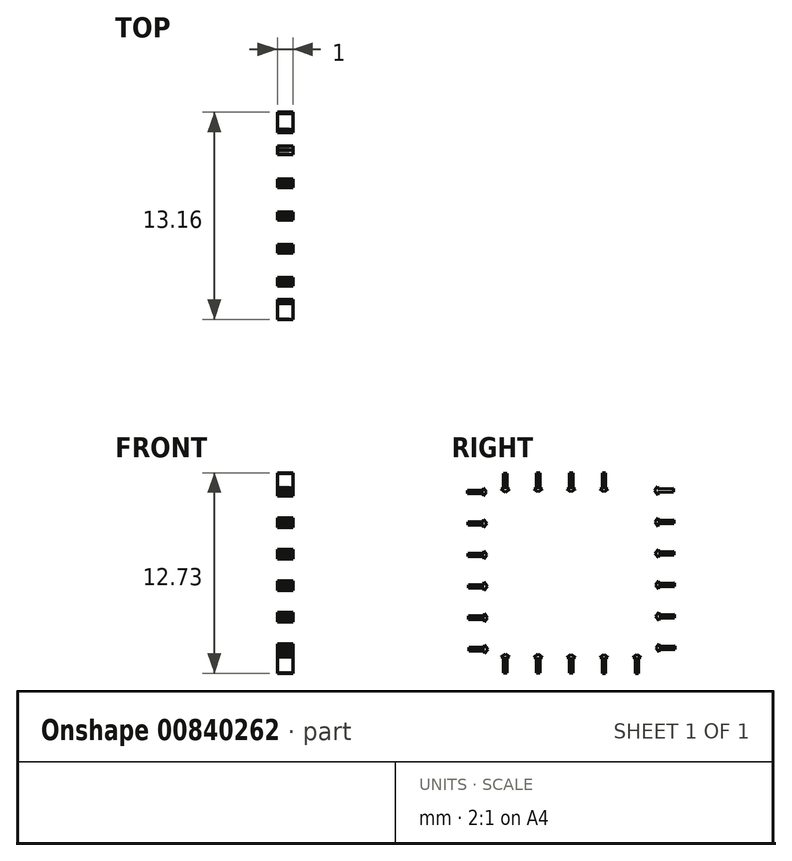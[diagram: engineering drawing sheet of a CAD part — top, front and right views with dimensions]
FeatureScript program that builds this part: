
annotation { "Feature Type Name" : "Feature", "Feature Type Description" : "" }
export const myFeature = defineFeature(function(context is Context, id is Id, definition is map)
    precondition{}
    {
        {
            var Q0;
            Q0=qCreatedBy(makeId("Right.planeOp"),FACE);
            var sketch = newSketch(context, id + "F0", { "sketchPlane" : qUnion([Q0])});
            skLineSegment(sketch, "E0.0.4.1", {"start": v(0.27, -10.76) * mm, "end": v(-0.73, -10.76) * mm});
            skLineSegment(sketch, "E1", {"start": v(1.47, -11.15) * mm, "end": v(1.47, -12.15) * mm});
            skLineSegment(sketch, "E2", {"start": v(-0.73, -10.76) * mm, "end": v(-0.73, -10.55) * mm});
            skLineSegment(sketch, "E3", {"start": v(-0.73, -10.55) * mm, "end": v(0.27, -10.55) * mm});
            skLineSegment(sketch, "E4", {"start": v(0.27, -10.55) * mm, "end": v(0.27, -10.39) * mm});
            skLineSegment(sketch, "E5", {"start": v(0.27, -10.76) * mm, "end": v(0.27, -10.92) * mm});
            skLineSegment(sketch, "E6", {"start": v(0.47, -10.65) * mm, "end": v(0.27, -10.39) * mm});
            skLineSegment(sketch, "E7", {"start": v(0.47, -10.65) * mm, "end": v(0.27, -10.92) * mm});
            skLineSegment(sketch, "E8.0.1.0", {"start": v(-0.75, -8.55) * mm, "end": v(0.25, -8.55) * mm});
            skLineSegment(sketch, "E8.0.1.1", {"start": v(0.25, -8.76) * mm, "end": v(-0.75, -8.76) * mm});
            skLineSegment(sketch, "E8.0.1.2", {"start": v(0.25, -8.76) * mm, "end": v(0.25, -8.92) * mm});
            skLineSegment(sketch, "E8.0.1.3", {"start": v(0.45, -8.65) * mm, "end": v(0.25, -8.92) * mm});
            skLineSegment(sketch, "E8.0.1.4", {"start": v(-0.75, -8.76) * mm, "end": v(-0.75, -8.55) * mm});
            skLineSegment(sketch, "E8.0.1.5", {"start": v(0.45, -8.65) * mm, "end": v(0.25, -8.39) * mm});
            skLineSegment(sketch, "E8.0.1.6", {"start": v(0.25, -8.55) * mm, "end": v(0.25, -8.39) * mm});
            skLineSegment(sketch, "E8.0.2.0", {"start": v(-0.77, -6.55) * mm, "end": v(0.24, -6.55) * mm});
            skLineSegment(sketch, "E8.0.2.1", {"start": v(0.24, -6.76) * mm, "end": v(-0.77, -6.76) * mm});
            skLineSegment(sketch, "E8.0.2.2", {"start": v(0.24, -6.76) * mm, "end": v(0.24, -6.92) * mm});
            skLineSegment(sketch, "E8.0.2.3", {"start": v(0.44, -6.66) * mm, "end": v(0.24, -6.92) * mm});
            skLineSegment(sketch, "E8.0.2.4", {"start": v(-0.77, -6.76) * mm, "end": v(-0.77, -6.55) * mm});
            skLineSegment(sketch, "E8.0.2.5", {"start": v(0.44, -6.66) * mm, "end": v(0.24, -6.39) * mm});
            skLineSegment(sketch, "E8.0.2.6", {"start": v(0.24, -6.55) * mm, "end": v(0.24, -6.39) * mm});
            skLineSegment(sketch, "E8.0.3.0", {"start": v(-0.78, -4.55) * mm, "end": v(0.22, -4.55) * mm});
            skLineSegment(sketch, "E8.0.3.1", {"start": v(0.22, -4.76) * mm, "end": v(-0.78, -4.76) * mm});
            skLineSegment(sketch, "E8.0.3.2", {"start": v(0.22, -4.76) * mm, "end": v(0.22, -4.92) * mm});
            skLineSegment(sketch, "E8.0.3.3", {"start": v(0.42, -4.66) * mm, "end": v(0.22, -4.92) * mm});
            skLineSegment(sketch, "E8.0.3.4", {"start": v(-0.78, -4.76) * mm, "end": v(-0.78, -4.55) * mm});
            skLineSegment(sketch, "E8.0.3.5", {"start": v(0.42, -4.66) * mm, "end": v(0.22, -4.4) * mm});
            skLineSegment(sketch, "E8.0.3.6", {"start": v(0.22, -4.55) * mm, "end": v(0.22, -4.4) * mm});
            skLineSegment(sketch, "E8.0.4.0", {"start": v(-0.8, -2.55) * mm, "end": v(0.2, -2.55) * mm});
            skLineSegment(sketch, "E8.0.4.1", {"start": v(0.2, -2.76) * mm, "end": v(-0.8, -2.76) * mm});
            skLineSegment(sketch, "E8.0.4.2", {"start": v(0.2, -2.76) * mm, "end": v(0.2, -2.92) * mm});
            skLineSegment(sketch, "E8.0.4.3", {"start": v(0.4, -2.66) * mm, "end": v(0.2, -2.92) * mm});
            skLineSegment(sketch, "E8.0.4.4", {"start": v(-0.8, -2.76) * mm, "end": v(-0.8, -2.55) * mm});
            skLineSegment(sketch, "E8.0.4.5", {"start": v(0.4, -2.66) * mm, "end": v(0.2, -2.4) * mm});
            skLineSegment(sketch, "E8.0.4.6", {"start": v(0.2, -2.55) * mm, "end": v(0.2, -2.4) * mm});
            skLineSegment(sketch, "E8.0.5.0", {"start": v(-0.81, -0.55) * mm, "end": v(0.2, -0.55) * mm});
            skLineSegment(sketch, "E8.0.5.1", {"start": v(0.2, -0.77) * mm, "end": v(-0.81, -0.77) * mm});
            skLineSegment(sketch, "E8.0.5.2", {"start": v(0.2, -0.77) * mm, "end": v(0.2, -0.93) * mm});
            skLineSegment(sketch, "E8.0.5.3", {"start": v(0.39, -0.66) * mm, "end": v(0.2, -0.93) * mm});
            skLineSegment(sketch, "E8.0.5.4", {"start": v(-0.81, -0.77) * mm, "end": v(-0.81, -0.55) * mm});
            skLineSegment(sketch, "E8.0.5.5", {"start": v(0.39, -0.66) * mm, "end": v(0.2, -0.4) * mm});
            skLineSegment(sketch, "E8.0.5.6", {"start": v(0.2, -0.55) * mm, "end": v(0.2, -0.4) * mm});
            skLineSegment(sketch, "E8.direction1", {"start": v(-0.73, -10.76) * mm, "end": v(24.27, -10.76) * mm, "construction": true});
            skLineSegment(sketch, "E8.direction2", {"start": v(-0.73, -10.76) * mm, "end": v(-0.75, -8.76) * mm, "construction": true});
            skLineSegment(sketch, "E9", {"start": v(1.47, -12.15) * mm, "end": v(1.68, -12.15) * mm});
            skLineSegment(sketch, "E10", {"start": v(1.68, -12.15) * mm, "end": v(1.68, -11.15) * mm});
            skLineSegment(sketch, "E11", {"start": v(1.47, -11.15) * mm, "end": v(1.3, -11.15) * mm});
            skLineSegment(sketch, "E12", {"start": v(1.68, -11.15) * mm, "end": v(1.84, -11.15) * mm});
            skLineSegment(sketch, "E13", {"start": v(1.58, -10.95) * mm, "end": v(1.3, -11.15) * mm});
            skLineSegment(sketch, "E14", {"start": v(1.58, -10.95) * mm, "end": v(1.84, -11.15) * mm});
            skLineSegment(sketch, "E15.1.0.0", {"start": v(3.56, -12.16) * mm, "end": v(3.77, -12.16) * mm});
            skLineSegment(sketch, "E15.1.0.1", {"start": v(3.67, -10.96) * mm, "end": v(3.4, -11.16) * mm});
            skLineSegment(sketch, "E15.1.0.2", {"start": v(3.56, -11.16) * mm, "end": v(3.4, -11.16) * mm});
            skLineSegment(sketch, "E15.1.0.3", {"start": v(3.77, -12.16) * mm, "end": v(3.77, -11.16) * mm});
            skLineSegment(sketch, "E15.1.0.4", {"start": v(3.67, -10.96) * mm, "end": v(3.93, -11.16) * mm});
            skLineSegment(sketch, "E15.1.0.5", {"start": v(3.56, -11.16) * mm, "end": v(3.56, -12.16) * mm});
            skLineSegment(sketch, "E15.1.0.6", {"start": v(3.77, -11.16) * mm, "end": v(3.93, -11.16) * mm});
            skLineSegment(sketch, "E15.2.0.0", {"start": v(5.65, -12.17) * mm, "end": v(5.86, -12.17) * mm});
            skLineSegment(sketch, "E15.2.0.1", {"start": v(5.76, -10.96) * mm, "end": v(5.5, -11.16) * mm});
            skLineSegment(sketch, "E15.2.0.2", {"start": v(5.65, -11.16) * mm, "end": v(5.5, -11.16) * mm});
            skLineSegment(sketch, "E15.2.0.3", {"start": v(5.86, -12.17) * mm, "end": v(5.86, -11.16) * mm});
            skLineSegment(sketch, "E15.2.0.4", {"start": v(5.76, -10.96) * mm, "end": v(6.02, -11.16) * mm});
            skLineSegment(sketch, "E15.2.0.5", {"start": v(5.65, -11.16) * mm, "end": v(5.65, -12.17) * mm});
            skLineSegment(sketch, "E15.2.0.6", {"start": v(5.86, -11.16) * mm, "end": v(6.02, -11.16) * mm});
            skLineSegment(sketch, "E15.3.0.0", {"start": v(7.74, -12.18) * mm, "end": v(7.95, -12.18) * mm});
            skLineSegment(sketch, "E15.3.0.1", {"start": v(7.85, -10.97) * mm, "end": v(7.58, -11.17) * mm});
            skLineSegment(sketch, "E15.3.0.2", {"start": v(7.74, -11.17) * mm, "end": v(7.58, -11.17) * mm});
            skLineSegment(sketch, "E15.3.0.3", {"start": v(7.95, -12.18) * mm, "end": v(7.95, -11.17) * mm});
            skLineSegment(sketch, "E15.3.0.4", {"start": v(7.85, -10.97) * mm, "end": v(8.11, -11.17) * mm});
            skLineSegment(sketch, "E15.3.0.5", {"start": v(7.74, -11.17) * mm, "end": v(7.74, -12.18) * mm});
            skLineSegment(sketch, "E15.3.0.6", {"start": v(7.95, -11.17) * mm, "end": v(8.11, -11.17) * mm});
            skLineSegment(sketch, "E15.4.0.0", {"start": v(9.83, -12.18) * mm, "end": v(10.04, -12.18) * mm});
            skLineSegment(sketch, "E15.4.0.1", {"start": v(9.94, -10.98) * mm, "end": v(9.67, -11.18) * mm});
            skLineSegment(sketch, "E15.4.0.2", {"start": v(9.83, -11.18) * mm, "end": v(9.67, -11.18) * mm});
            skLineSegment(sketch, "E15.4.0.3", {"start": v(10.04, -12.18) * mm, "end": v(10.04, -11.18) * mm});
            skLineSegment(sketch, "E15.4.0.4", {"start": v(9.94, -10.98) * mm, "end": v(10.2, -11.18) * mm});
            skLineSegment(sketch, "E15.4.0.5", {"start": v(9.83, -11.18) * mm, "end": v(9.83, -12.18) * mm});
            skLineSegment(sketch, "E15.4.0.6", {"start": v(10.04, -11.18) * mm, "end": v(10.2, -11.18) * mm});
            skLineSegment(sketch, "E15.direction1", {"start": v(1.47, -12.15) * mm, "end": v(3.56, -12.16) * mm, "construction": true});
            skLineSegment(sketch, "E16.MirrorCS", {"start": v(11.14, -10.57) * mm, "end": v(11.35, -10.83) * mm});
            skLineSegment(sketch, "E17.MirrorCS", {"start": v(11.14, -10.57) * mm, "end": v(11.34, -10.3) * mm});
            skLineSegment(sketch, "E18.MirrorCS", {"start": v(11.34, -10.67) * mm, "end": v(11.35, -10.83) * mm});
            skLineSegment(sketch, "E19.MirrorCS", {"start": v(11.34, -10.46) * mm, "end": v(11.34, -10.3) * mm});
            skLineSegment(sketch, "E20.MirrorCS", {"start": v(11.33, -8.67) * mm, "end": v(11.33, -8.83) * mm});
            skLineSegment(sketch, "E21.MirrorCS", {"start": v(11.13, -8.57) * mm, "end": v(11.32, -8.3) * mm});
            skLineSegment(sketch, "E22.MirrorCS", {"start": v(12.35, -10.65) * mm, "end": v(12.35, -10.44) * mm});
            skLineSegment(sketch, "E23.MirrorCS", {"start": v(11.33, -8.46) * mm, "end": v(11.32, -8.3) * mm});
            skLineSegment(sketch, "E24.MirrorCS", {"start": v(11.06, -0.57) * mm, "end": v(11.26, -0.3) * mm});
            skLineSegment(sketch, "E25.MirrorCS", {"start": v(11.06, -0.57) * mm, "end": v(11.27, -0.84) * mm});
            skLineSegment(sketch, "E26.MirrorCS", {"start": v(11.3, -4.46) * mm, "end": v(11.3, -4.3) * mm});
            skLineSegment(sketch, "E27.MirrorCS", {"start": v(11.26, -0.68) * mm, "end": v(11.27, -0.84) * mm});
            skLineSegment(sketch, "E28.MirrorCS", {"start": v(11.08, -2.57) * mm, "end": v(11.27, -2.3) * mm});
            skLineSegment(sketch, "E29.MirrorCS", {"start": v(11.11, -6.57) * mm, "end": v(11.3, -6.3) * mm});
            skLineSegment(sketch, "E30.MirrorCS", {"start": v(11.1, -4.57) * mm, "end": v(11.3, -4.3) * mm});
            skLineSegment(sketch, "E31.MirrorCS", {"start": v(11.3, -4.67) * mm, "end": v(11.3, -4.83) * mm});
            skLineSegment(sketch, "E32.MirrorCS", {"start": v(12.33, -8.65) * mm, "end": v(12.33, -8.44) * mm});
            skLineSegment(sketch, "E33.MirrorCS", {"start": v(11.3, -6.46) * mm, "end": v(11.3, -6.3) * mm});
            skLineSegment(sketch, "E34.MirrorCS", {"start": v(11.31, -6.67) * mm, "end": v(11.31, -6.83) * mm});
            skLineSegment(sketch, "E35.MirrorCS", {"start": v(11.1, -4.57) * mm, "end": v(11.3, -4.83) * mm});
            skLineSegment(sketch, "E36.MirrorCS", {"start": v(11.28, -2.67) * mm, "end": v(11.28, -2.83) * mm});
            skLineSegment(sketch, "E37.MirrorCS", {"start": v(11.11, -6.57) * mm, "end": v(11.31, -6.83) * mm});
            skLineSegment(sketch, "E38.MirrorCS", {"start": v(11.08, -2.57) * mm, "end": v(11.28, -2.83) * mm});
            skLineSegment(sketch, "E39.MirrorCS", {"start": v(11.13, -8.57) * mm, "end": v(11.33, -8.83) * mm});
            skLineSegment(sketch, "E40.MirrorCS", {"start": v(11.26, -0.46) * mm, "end": v(11.26, -0.3) * mm});
            skLineSegment(sketch, "E41.MirrorCS", {"start": v(12.3, -4.66) * mm, "end": v(12.3, -4.44) * mm});
            skLineSegment(sketch, "E42.MirrorCS", {"start": v(12.32, -6.66) * mm, "end": v(12.31, -6.44) * mm});
            skLineSegment(sketch, "E43.MirrorCS", {"start": v(12.27, -0.66) * mm, "end": v(12.27, -0.45) * mm});
            skLineSegment(sketch, "E44.MirrorCS", {"start": v(11.28, -2.46) * mm, "end": v(11.27, -2.3) * mm});
            skLineSegment(sketch, "E45.MirrorCS", {"start": v(12.28, -2.66) * mm, "end": v(12.28, -2.45) * mm});
            skLineSegment(sketch, "E46.MirrorCS", {"start": v(12.31, -6.44) * mm, "end": v(11.3, -6.46) * mm});
            skLineSegment(sketch, "E47.MirrorCS", {"start": v(11.3, -4.67) * mm, "end": v(12.3, -4.66) * mm});
            skLineSegment(sketch, "E48.MirrorCS", {"start": v(12.3, -4.44) * mm, "end": v(11.3, -4.46) * mm});
            skLineSegment(sketch, "E49.MirrorCS", {"start": v(12.35, -10.44) * mm, "end": v(11.34, -10.46) * mm});
            skLineSegment(sketch, "E50.MirrorCS", {"start": v(11.28, -2.67) * mm, "end": v(12.28, -2.66) * mm});
            skLineSegment(sketch, "E51.MirrorCS", {"start": v(11.33, -8.67) * mm, "end": v(12.33, -8.65) * mm});
            skLineSegment(sketch, "E52.MirrorCS", {"start": v(11.26, -0.68) * mm, "end": v(12.27, -0.66) * mm});
            skLineSegment(sketch, "E53.MirrorCS", {"start": v(11.31, -6.67) * mm, "end": v(12.32, -6.66) * mm});
            skLineSegment(sketch, "E54.MirrorCS", {"start": v(12.35, -10.65) * mm, "end": v(12.33, -8.65) * mm, "construction": true});
            skLineSegment(sketch, "E55.MirrorCS", {"start": v(12.28, -2.45) * mm, "end": v(11.28, -2.46) * mm});
            skLineSegment(sketch, "E56.MirrorCS", {"start": v(12.27, -0.45) * mm, "end": v(11.26, -0.46) * mm});
            skLineSegment(sketch, "E57.MirrorCS", {"start": v(11.34, -10.67) * mm, "end": v(12.35, -10.65) * mm});
            skLineSegment(sketch, "E58.MirrorCS", {"start": v(12.33, -8.44) * mm, "end": v(11.33, -8.46) * mm});
            skLineSegment(sketch, "E59.MirrorCS", {"start": v(5.76, -0.66) * mm, "end": v(6.02, -0.46) * mm});
            skLineSegment(sketch, "E60.MirrorCS", {"start": v(5.86, -0.46) * mm, "end": v(6.02, -0.46) * mm});
            skLineSegment(sketch, "E61.MirrorCS", {"start": v(7.85, -0.66) * mm, "end": v(7.58, -0.46) * mm});
            skLineSegment(sketch, "E62.MirrorCS", {"start": v(3.56, 0.53) * mm, "end": v(3.77, 0.53) * mm});
            skLineSegment(sketch, "E63.MirrorCS", {"start": v(3.67, -0.67) * mm, "end": v(3.4, -0.47) * mm});
            skLineSegment(sketch, "E64.MirrorCS", {"start": v(1.47, -0.48) * mm, "end": v(1.3, -0.48) * mm});
            skLineSegment(sketch, "E65.MirrorCS", {"start": v(1.58, -0.68) * mm, "end": v(1.84, -0.48) * mm});
            skLineSegment(sketch, "E66.MirrorCS", {"start": v(7.74, -0.46) * mm, "end": v(7.58, -0.46) * mm});
            skLineSegment(sketch, "E67.MirrorCS", {"start": v(7.95, -0.46) * mm, "end": v(8.11, -0.46) * mm});
            skLineSegment(sketch, "E68.MirrorCS", {"start": v(5.65, -0.46) * mm, "end": v(5.5, -0.46) * mm});
            skLineSegment(sketch, "E69.MirrorCS", {"start": v(1.47, 0.52) * mm, "end": v(1.68, 0.52) * mm});
            skLineSegment(sketch, "E70.MirrorCS", {"start": v(1.58, -0.68) * mm, "end": v(1.3, -0.48) * mm});
            skLineSegment(sketch, "E71.MirrorCS", {"start": v(3.56, -0.47) * mm, "end": v(3.4, -0.47) * mm});
            skLineSegment(sketch, "E72.MirrorCS", {"start": v(7.85, -0.66) * mm, "end": v(8.11, -0.46) * mm});
            skLineSegment(sketch, "E73.MirrorCS", {"start": v(1.68, -0.48) * mm, "end": v(1.84, -0.48) * mm});
            skLineSegment(sketch, "E74.MirrorCS", {"start": v(5.76, -0.66) * mm, "end": v(5.5, -0.46) * mm});
            skLineSegment(sketch, "E75.MirrorCS", {"start": v(5.65, 0.54) * mm, "end": v(5.86, 0.54) * mm});
            skLineSegment(sketch, "E76.MirrorCS", {"start": v(7.74, 0.55) * mm, "end": v(7.95, 0.55) * mm});
            skLineSegment(sketch, "E77.MirrorCS", {"start": v(3.67, -0.67) * mm, "end": v(3.93, -0.47) * mm});
            skLineSegment(sketch, "E78.MirrorCS", {"start": v(3.77, -0.47) * mm, "end": v(3.93, -0.47) * mm});
            skLineSegment(sketch, "E79.MirrorCS", {"start": v(5.86, 0.54) * mm, "end": v(5.86, -0.46) * mm});
            skLineSegment(sketch, "E80.MirrorCS", {"start": v(5.65, -0.46) * mm, "end": v(5.65, 0.54) * mm});
            skLineSegment(sketch, "E81.MirrorCS", {"start": v(1.47, -0.48) * mm, "end": v(1.47, 0.52) * mm});
            skLineSegment(sketch, "E82.MirrorCS", {"start": v(1.47, 0.52) * mm, "end": v(3.56, 0.53) * mm, "construction": true});
            skLineSegment(sketch, "E83.MirrorCS", {"start": v(7.74, -0.46) * mm, "end": v(7.74, 0.55) * mm});
            skLineSegment(sketch, "E84.MirrorCS", {"start": v(3.77, 0.53) * mm, "end": v(3.77, -0.47) * mm});
            skLineSegment(sketch, "E85.MirrorCS", {"start": v(1.68, 0.52) * mm, "end": v(1.68, -0.48) * mm});
            skLineSegment(sketch, "E86.MirrorCS", {"start": v(3.56, -0.47) * mm, "end": v(3.56, 0.53) * mm});
            skLineSegment(sketch, "E87.MirrorCS", {"start": v(7.95, 0.55) * mm, "end": v(7.95, -0.46) * mm});
            skSolve(sketch);
        }
        {
            var Q0;
            Q0=makeQuery(id+"F0.imprint","IMPRINT",FACE,{"disambiguationData":[TD([[makeQuery(id+"F0.imprint","IMPRINT",EDGE,{"derivedFrom":sQuery(id+"F0.wireOp",EDGE,"b7051014-9e5f-4858-866f-d238a0f6af6c.0.1.1")}),1.0]])]});
            var Q1;
            Q1=makeQuery(id+"F0.imprint","IMPRINT",FACE,{"disambiguationData":[TD([[makeQuery(id+"F0.imprint","IMPRINT",EDGE,{"derivedFrom":sQuery(id+"F0.wireOp",EDGE,"9d555bab-859a-4ead-993f-75c362023f64.2.0")}),-1.0]])]});
            var Q2;
            Q2=makeQuery(id+"F0.imprint","IMPRINT",FACE,{"disambiguationData":[TD([[makeQuery(id+"F0.imprint","IMPRINT",EDGE,{"derivedFrom":sQuery(id+"F0.wireOp",EDGE,"E0.0.3.1")}),-1.0]])]});
            var Q3;
            Q3=makeQuery(id+"F0.imprint","IMPRINT",FACE,{"disambiguationData":[TD([[makeQuery(id+"F0.imprint","IMPRINT",EDGE,{"derivedFrom":sQuery(id+"F0.wireOp",EDGE,"f600e33e-be41-4db6-be2c-c8745f93fd9a.0.2.0")}),-1.0]])]});
            var Q4;
            Q4=makeQuery(id+"F0.imprint","IMPRINT",FACE,{"disambiguationData":[TD([[makeQuery(id+"F0.imprint","IMPRINT",EDGE,{"derivedFrom":sQuery(id+"F0.wireOp",EDGE,"f600e33e-be41-4db6-be2c-c8745f93fd9a.0.3.0")}),-1.0]])]});
            var Q5;
            Q5=makeQuery(id+"F0.imprint","IMPRINT",FACE,{"disambiguationData":[TD([[makeQuery(id+"F0.imprint","IMPRINT",EDGE,{"derivedFrom":sQuery(id+"F0.wireOp",EDGE,"f600e33e-be41-4db6-be2c-c8745f93fd9a.0.4.0")}),-1.0]])]});
            var Q6;
            Q6=makeQuery(id+"F0.imprint","IMPRINT",FACE,{"disambiguationData":[TD([[makeQuery(id+"F0.imprint","IMPRINT",EDGE,{"derivedFrom":sQuery(id+"F0.wireOp",EDGE,"b7051014-9e5f-4858-866f-d238a0f6af6c.0.2.1")}),1.0]])]});
            var Q7;
            Q7=makeQuery(id+"F0.imprint","IMPRINT",FACE,{"disambiguationData":[TD([[makeQuery(id+"F0.imprint","IMPRINT",EDGE,{"derivedFrom":sQuery(id+"F0.wireOp",EDGE,"E0.0.4.1")}),-1.0]])]});
            var Q8;
            Q8=makeQuery(id+"F0.imprint","IMPRINT",FACE,{"disambiguationData":[TD([[makeQuery(id+"F0.imprint","IMPRINT",EDGE,{"derivedFrom":sQuery(id+"F0.wireOp",EDGE,"f600e33e-be41-4db6-be2c-c8745f93fd9a.0.1.0")}),-1.0]])]});
            var Q9;
            Q9=makeQuery(id+"F0.imprint","IMPRINT",FACE,{"disambiguationData":[TD([[makeQuery(id+"F0.imprint","IMPRINT",EDGE,{"derivedFrom":sQuery(id+"F0.wireOp",EDGE,"a764017d-9780-4a7a-a1af-faccf4d78144.2.0.0")}),1.0]])]});
            var Q10;
            Q10=makeQuery(id+"F0.imprint","IMPRINT",FACE,{"disambiguationData":[TD([[makeQuery(id+"F0.imprint","IMPRINT",EDGE,{"derivedFrom":sQuery(id+"F0.wireOp",EDGE,"a764017d-9780-4a7a-a1af-faccf4d78144.5.0.0")}),1.0]])]});
            var Q11;
            Q11=makeQuery(id+"F0.imprint","IMPRINT",FACE,{"disambiguationData":[TD([[makeQuery(id+"F0.imprint","IMPRINT",EDGE,{"derivedFrom":sQuery(id+"F0.wireOp",EDGE,"44ae7ea8-8850-4e7e-a8f5-5314db1a9b29.5.0.0")}),1.0]])]});
            var Q12;
            Q12=makeQuery(id+"F0.imprint","IMPRINT",FACE,{"disambiguationData":[TD([[makeQuery(id+"F0.imprint","IMPRINT",EDGE,{"derivedFrom":sQuery(id+"F0.wireOp",EDGE,"E0.0.1.1")}),-1.0]])]});
            var Q13;
            Q13=makeQuery(id+"F0.imprint","IMPRINT",FACE,{"disambiguationData":[TD([[makeQuery(id+"F0.imprint","IMPRINT",EDGE,{"derivedFrom":sQuery(id+"F0.wireOp",EDGE,"44ae7ea8-8850-4e7e-a8f5-5314db1a9b29.4.0.0")}),1.0]])]});
            var Q14;
            Q14=makeQuery(id+"F0.imprint","IMPRINT",FACE,{"disambiguationData":[TD([[makeQuery(id+"F0.imprint","IMPRINT",EDGE,{"derivedFrom":sQuery(id+"F0.wireOp",EDGE,"a764017d-9780-4a7a-a1af-faccf4d78144.1.0.0")}),1.0]])]});
            var Q15;
            Q15=makeQuery(id+"F0.imprint","IMPRINT",FACE,{"disambiguationData":[TD([[makeQuery(id+"F0.imprint","IMPRINT",EDGE,{"derivedFrom":sQuery(id+"F0.wireOp",EDGE,"E1")}),1.0]])]});
            var Q16;
            Q16=makeQuery(id+"F0.imprint","IMPRINT",FACE,{"disambiguationData":[TD([[makeQuery(id+"F0.imprint","IMPRINT",EDGE,{"derivedFrom":sQuery(id+"F0.wireOp",EDGE,"a764017d-9780-4a7a-a1af-faccf4d78144.4.0.0")}),1.0]])]});
            var Q17;
            Q17=makeQuery(id+"F0.imprint","IMPRINT",FACE,{"disambiguationData":[TD([[makeQuery(id+"F0.imprint","IMPRINT",EDGE,{"derivedFrom":sQuery(id+"F0.wireOp",EDGE,"4c1bbaaa-0e02-4e0d-9e7d-ec6760599301.4.0")}),-1.0]])]});
            var Q18;
            Q18=makeQuery(id+"F0.imprint","IMPRINT",FACE,{"disambiguationData":[TD([[makeQuery(id+"F0.imprint","IMPRINT",EDGE,{"derivedFrom":sQuery(id+"F0.wireOp",EDGE,"b6f42888-3161-477c-80ad-e87b3ed1a3cd.0.2.2")}),1.0]])]});
            var Q19;
            Q19=makeQuery(id+"F0.imprint","IMPRINT",FACE,{"disambiguationData":[TD([[makeQuery(id+"F0.imprint","IMPRINT",EDGE,{"derivedFrom":sQuery(id+"F0.wireOp",EDGE,"a764017d-9780-4a7a-a1af-faccf4d78144.3.0.0")}),1.0]])]});
            var Q20;
            Q20=makeQuery(id+"F0.imprint","IMPRINT",FACE,{"disambiguationData":[TD([[makeQuery(id+"F0.imprint","IMPRINT",EDGE,{"derivedFrom":sQuery(id+"F0.wireOp",EDGE,"44ae7ea8-8850-4e7e-a8f5-5314db1a9b29.3.0.0")}),1.0]])]});
            var Q21;
            Q21=makeQuery(id+"F0.imprint","IMPRINT",FACE,{"disambiguationData":[TD([[makeQuery(id+"F0.imprint","IMPRINT",EDGE,{"derivedFrom":sQuery(id+"F0.wireOp",EDGE,"a764017d-9780-4a7a-a1af-faccf4d78144.2.0.2")}),1.0]])]});
            var Q22;
            Q22=makeQuery(id+"F0.imprint","IMPRINT",FACE,{"disambiguationData":[TD([[makeQuery(id+"F0.imprint","IMPRINT",EDGE,{"derivedFrom":sQuery(id+"F0.wireOp",EDGE,"44ae7ea8-8850-4e7e-a8f5-5314db1a9b29.2.0.0")}),1.0]])]});
            var Q23;
            Q23=makeQuery(id+"F0.imprint","IMPRINT",FACE,{"disambiguationData":[TD([[makeQuery(id+"F0.imprint","IMPRINT",EDGE,{"derivedFrom":sQuery(id+"F0.wireOp",EDGE,"E0.0.1.0")}),1.0]])]});
            var Q24;
            Q24=makeQuery(id+"F0.imprint","IMPRINT",FACE,{"disambiguationData":[TD([[makeQuery(id+"F0.imprint","IMPRINT",EDGE,{"derivedFrom":sQuery(id+"F0.wireOp",EDGE,"9d555bab-859a-4ead-993f-75c362023f64.2.1")}),-1.0]])]});
            var Q25;
            Q25=makeQuery(id+"F0.imprint","IMPRINT",FACE,{"disambiguationData":[TD([[makeQuery(id+"F0.imprint","IMPRINT",EDGE,{"derivedFrom":sQuery(id+"F0.wireOp",EDGE,"be805554-1628-4050-af92-f406b947808e")}),1.0]])]});
            var Q26;
            Q26=makeQuery(id+"F0.imprint","IMPRINT",FACE,{"disambiguationData":[TD([[makeQuery(id+"F0.imprint","IMPRINT",EDGE,{"derivedFrom":sQuery(id+"F0.wireOp",EDGE,"b6f42888-3161-477c-80ad-e87b3ed1a3cd.0.1.2")}),1.0]])]});
            var Q27;
            Q27=makeQuery(id+"F0.imprint","IMPRINT",FACE,{"disambiguationData":[TD([[makeQuery(id+"F0.imprint","IMPRINT",EDGE,{"derivedFrom":sQuery(id+"F0.wireOp",EDGE,"E0.0.2.1")}),-1.0]])]});
            var Q28;
            Q28=makeQuery(id+"F0.imprint","IMPRINT",FACE,{"disambiguationData":[TD([[makeQuery(id+"F0.imprint","IMPRINT",EDGE,{"derivedFrom":sQuery(id+"F0.wireOp",EDGE,"44ae7ea8-8850-4e7e-a8f5-5314db1a9b29.1.0.0")}),1.0]])]});
            var Q29;
            Q29=makeQuery(id+"F0.imprint","IMPRINT",FACE,{"disambiguationData":[TD([[makeQuery(id+"F0.imprint","IMPRINT",EDGE,{"derivedFrom":sQuery(id+"F0.wireOp",EDGE,"beb71ddb-0849-4b39-bbed-d1b6f0a080cd.6.6.0")}),1.0]])]});
            var Q30;
            Q30=makeQuery(id+"F0.imprint","IMPRINT",FACE,{"disambiguationData":[TD([[makeQuery(id+"F0.imprint","IMPRINT",EDGE,{"derivedFrom":sQuery(id+"F0.wireOp",EDGE,"b7051014-9e5f-4858-866f-d238a0f6af6c.0.1.0")}),1.0]])]});
            var Q31;
            Q31=makeQuery(id+"F0.imprint","IMPRINT",FACE,{"disambiguationData":[TD([[makeQuery(id+"F0.imprint","IMPRINT",EDGE,{"derivedFrom":sQuery(id+"F0.wireOp",EDGE,"beb71ddb-0849-4b39-bbed-d1b6f0a080cd.3.6.0")}),-1.0]])]});
            var Q32;
            Q32=makeQuery(id+"F0.imprint","IMPRINT",FACE,{"disambiguationData":[TD([[makeQuery(id+"F0.imprint","IMPRINT",EDGE,{"derivedFrom":sQuery(id+"F0.wireOp",EDGE,"a764017d-9780-4a7a-a1af-faccf4d78144.1.0.2")}),1.0]])]});
            var Q33;
            Q33=makeQuery(id+"F0.imprint","IMPRINT",FACE,{"disambiguationData":[TD([[makeQuery(id+"F0.imprint","IMPRINT",EDGE,{"derivedFrom":sQuery(id+"F0.wireOp",EDGE,"a764017d-9780-4a7a-a1af-faccf4d78144.5.0.2")}),1.0]])]});
            var Q34;
            Q34=makeQuery(id+"F0.imprint","IMPRINT",FACE,{"disambiguationData":[TD([[makeQuery(id+"F0.imprint","IMPRINT",EDGE,{"derivedFrom":sQuery(id+"F0.wireOp",EDGE,"44ae7ea8-8850-4e7e-a8f5-5314db1a9b29.4.0.3")}),-1.0]])]});
            var Q35;
            Q35=makeQuery(id+"F0.imprint","IMPRINT",FACE,{"disambiguationData":[TD([[makeQuery(id+"F0.imprint","IMPRINT",EDGE,{"derivedFrom":sQuery(id+"F0.wireOp",EDGE,"44ae7ea8-8850-4e7e-a8f5-5314db1a9b29.5.0.3")}),-1.0]])]});
            var Q36;
            Q36=makeQuery(id+"F0.imprint","IMPRINT",FACE,{"disambiguationData":[TD([[makeQuery(id+"F0.imprint","IMPRINT",EDGE,{"derivedFrom":sQuery(id+"F0.wireOp",EDGE,"44ae7ea8-8850-4e7e-a8f5-5314db1a9b29.1.0.3")}),-1.0]])]});
            var Q37;
            Q37=makeQuery(id+"F0.imprint","IMPRINT",FACE,{"disambiguationData":[TD([[makeQuery(id+"F0.imprint","IMPRINT",EDGE,{"derivedFrom":sQuery(id+"F0.wireOp",EDGE,"b6f42888-3161-477c-80ad-e87b3ed1a3cd.0.1.0")}),1.0]])]});
            var Q38;
            Q38=makeQuery(id+"F0.imprint","IMPRINT",FACE,{"disambiguationData":[TD([[makeQuery(id+"F0.imprint","IMPRINT",EDGE,{"derivedFrom":sQuery(id+"F0.wireOp",EDGE,"a764017d-9780-4a7a-a1af-faccf4d78144.4.0.2")}),1.0]])]});
            var Q39;
            {var subQ3=sQuery(id+"F0.wireOp",EDGE,"f600e33e-be41-4db6-be2c-c8745f93fd9a.0.1.0");Q39=makeQuery(id+"F0.imprint","IMPRINT",FACE,{"disambiguationData":[TD([[makeQuery(id+"F0.imprint","IMPRINT",EDGE,{"derivedFrom":subQ3}),1.0]])]});}
            var Q40;
            Q40=makeQuery(id+"F0.imprint","IMPRINT",FACE,{"disambiguationData":[TD([[makeQuery(id+"F0.imprint","IMPRINT",EDGE,{"derivedFrom":sQuery(id+"F0.wireOp",EDGE,"E0.0.2.0")}),1.0]])]});
            var Q41;
            Q41=makeQuery(id+"F0.imprint","IMPRINT",FACE,{"disambiguationData":[TD([[makeQuery(id+"F0.imprint","IMPRINT",EDGE,{"derivedFrom":sQuery(id+"F0.wireOp",EDGE,"b6f42888-3161-477c-80ad-e87b3ed1a3cd.0.2.0")}),1.0]])]});
            var Q42;
            Q42=makeQuery(id+"F0.imprint","IMPRINT",FACE,{"disambiguationData":[TD([[makeQuery(id+"F0.imprint","IMPRINT",EDGE,{"derivedFrom":sQuery(id+"F0.wireOp",EDGE,"44ae7ea8-8850-4e7e-a8f5-5314db1a9b29.3.0.3")}),-1.0]])]});
            var Q43;
            Q43=makeQuery(id+"F0.imprint","IMPRINT",FACE,{"disambiguationData":[TD([[makeQuery(id+"F0.imprint","IMPRINT",EDGE,{"derivedFrom":sQuery(id+"F0.wireOp",EDGE,"44ae7ea8-8850-4e7e-a8f5-5314db1a9b29.2.0.3")}),-1.0]])]});
            var Q44;
            Q44=makeQuery(id+"F0.imprint","IMPRINT",FACE,{"disambiguationData":[TD([[makeQuery(id+"F0.imprint","IMPRINT",EDGE,{"derivedFrom":sQuery(id+"F0.wireOp",EDGE,"f600e33e-be41-4db6-be2c-c8745f93fd9a.0.2.0")}),1.0]])]});
            var Q45;
            Q45=makeQuery(id+"F0.imprint","IMPRINT",FACE,{"disambiguationData":[TD([[makeQuery(id+"F0.imprint","IMPRINT",EDGE,{"derivedFrom":sQuery(id+"F0.wireOp",EDGE,"f600e33e-be41-4db6-be2c-c8745f93fd9a.0.4.0")}),1.0]])]});
            var Q46;
            Q46=makeQuery(id+"F0.imprint","IMPRINT",FACE,{"disambiguationData":[TD([[makeQuery(id+"F0.imprint","IMPRINT",EDGE,{"derivedFrom":sQuery(id+"F0.wireOp",EDGE,"a764017d-9780-4a7a-a1af-faccf4d78144.3.0.2")}),1.0]])]});
            var Q47;
            Q47=makeQuery(id+"F0.imprint","IMPRINT",FACE,{"disambiguationData":[TD([[makeQuery(id+"F0.imprint","IMPRINT",EDGE,{"derivedFrom":sQuery(id+"F0.wireOp",EDGE,"4c1bbaaa-0e02-4e0d-9e7d-ec6760599301.4.1")}),-1.0]])]});
            var Q48;
            Q48=makeQuery(id+"F0.imprint","IMPRINT",FACE,{"disambiguationData":[TD([[makeQuery(id+"F0.imprint","IMPRINT",EDGE,{"derivedFrom":sQuery(id+"F0.wireOp",EDGE,"f600e33e-be41-4db6-be2c-c8745f93fd9a.0.3.0")}),1.0]])]});
            var Q49;
            Q49=makeQuery(id+"F0.imprint","IMPRINT",FACE,{"disambiguationData":[TD([[makeQuery(id+"F0.imprint","IMPRINT",EDGE,{"derivedFrom":sQuery(id+"F0.wireOp",EDGE,"b7051014-9e5f-4858-866f-d238a0f6af6c.0.2.0")}),1.0]])]});
            var Q50;
            Q50=makeQuery(id+"F0.imprint","IMPRINT",FACE,{"disambiguationData":[TD([[makeQuery(id+"F0.imprint","IMPRINT",EDGE,{"derivedFrom":sQuery(id+"F0.wireOp",EDGE,"E0.0.3.0")}),1.0]])]});
            var Q51;
            Q51=makeQuery(id+"F0.imprint","IMPRINT",FACE,{"disambiguationData":[TD([[makeQuery(id+"F0.imprint","IMPRINT",EDGE,{"derivedFrom":sQuery(id+"F0.wireOp",EDGE,"E0.0.4.0")}),1.0]])]});
            var Q52;
            Q52=makeQuery(id+"F0.imprint","IMPRINT",FACE,{"disambiguationData":[TD([[makeQuery(id+"F0.imprint","IMPRINT",EDGE,{"derivedFrom":sQuery(id+"F0.wireOp",EDGE,"E15.1.0.0")}),1.0]])]});
            var Q53;
            Q53=makeQuery(id+"F0.imprint","IMPRINT",FACE,{"disambiguationData":[TD([[makeQuery(id+"F0.imprint","IMPRINT",EDGE,{"derivedFrom":sQuery(id+"F0.wireOp",EDGE,"E15.2.0.0")}),1.0]])]});
            var Q54;
            Q54=makeQuery(id+"F0.imprint","IMPRINT",FACE,{"disambiguationData":[TD([[makeQuery(id+"F0.imprint","IMPRINT",EDGE,{"derivedFrom":sQuery(id+"F0.wireOp",EDGE,"E15.3.0.0")}),1.0]])]});
            var Q55;
            Q55=makeQuery(id+"F0.imprint","IMPRINT",FACE,{"disambiguationData":[TD([[makeQuery(id+"F0.imprint","IMPRINT",EDGE,{"derivedFrom":sQuery(id+"F0.wireOp",EDGE,"E15.4.0.0")}),1.0]])]});
            var Q56;
            Q56=makeQuery(id+"F0.imprint","IMPRINT",FACE,{"disambiguationData":[TD([[makeQuery(id+"F0.imprint","IMPRINT",EDGE,{"derivedFrom":sQuery(id+"F0.wireOp",EDGE,"E16.MirrorCS")}),1.0]])]});
            var Q57;
            Q57=makeQuery(id+"F0.imprint","IMPRINT",FACE,{"disambiguationData":[TD([[makeQuery(id+"F0.imprint","IMPRINT",EDGE,{"derivedFrom":sQuery(id+"F0.wireOp",EDGE,"E20.MirrorCS")}),-1.0]])]});
            var Q58;
            Q58=makeQuery(id+"F0.imprint","IMPRINT",FACE,{"disambiguationData":[TD([[makeQuery(id+"F0.imprint","IMPRINT",EDGE,{"derivedFrom":sQuery(id+"F0.wireOp",EDGE,"E29.MirrorCS")}),-1.0]])]});
            var Q59;
            Q59=makeQuery(id+"F0.imprint","IMPRINT",FACE,{"disambiguationData":[TD([[makeQuery(id+"F0.imprint","IMPRINT",EDGE,{"derivedFrom":sQuery(id+"F0.wireOp",EDGE,"E26.MirrorCS")}),1.0]])]});
            var Q60;
            Q60=makeQuery(id+"F0.imprint","IMPRINT",FACE,{"disambiguationData":[TD([[makeQuery(id+"F0.imprint","IMPRINT",EDGE,{"derivedFrom":sQuery(id+"F0.wireOp",EDGE,"E28.MirrorCS")}),-1.0]])]});
            var Q61;
            Q61=makeQuery(id+"F0.imprint","IMPRINT",FACE,{"disambiguationData":[TD([[makeQuery(id+"F0.imprint","IMPRINT",EDGE,{"derivedFrom":sQuery(id+"F0.wireOp",EDGE,"E24.MirrorCS")}),-1.0]])]});
            var Q62;
            Q62=makeQuery(id+"F0.imprint","IMPRINT",FACE,{"disambiguationData":[TD([[makeQuery(id+"F0.imprint","IMPRINT",EDGE,{"derivedFrom":sQuery(id+"F0.wireOp",EDGE,"E61.MirrorCS")}),-1.0]])]});
            var Q63;
            Q63=makeQuery(id+"F0.imprint","IMPRINT",FACE,{"disambiguationData":[TD([[makeQuery(id+"F0.imprint","IMPRINT",EDGE,{"derivedFrom":sQuery(id+"F0.wireOp",EDGE,"E59.MirrorCS")}),1.0]])]});
            var Q64;
            Q64=makeQuery(id+"F0.imprint","IMPRINT",FACE,{"disambiguationData":[TD([[makeQuery(id+"F0.imprint","IMPRINT",EDGE,{"derivedFrom":sQuery(id+"F0.wireOp",EDGE,"E62.MirrorCS")}),-1.0]])]});
            var Q65;
            Q65=makeQuery(id+"F0.imprint","IMPRINT",FACE,{"disambiguationData":[TD([[makeQuery(id+"F0.imprint","IMPRINT",EDGE,{"derivedFrom":sQuery(id+"F0.wireOp",EDGE,"E64.MirrorCS")}),1.0]])]});
            var Q66;
            Q66=makeQuery(id+"F0.imprint","IMPRINT",FACE,{"disambiguationData":[TD([[makeQuery(id+"F0.imprint","IMPRINT",EDGE,{"derivedFrom":sQuery(id+"F0.wireOp",EDGE,"E8.0.5.0")}),-1.0]])]});
            var Q67;
            Q67=makeQuery(id+"F0.imprint","IMPRINT",FACE,{"disambiguationData":[TD([[makeQuery(id+"F0.imprint","IMPRINT",EDGE,{"derivedFrom":sQuery(id+"F0.wireOp",EDGE,"E8.0.4.0")}),-1.0]])]});
            var Q68;
            Q68=makeQuery(id+"F0.imprint","IMPRINT",FACE,{"disambiguationData":[TD([[makeQuery(id+"F0.imprint","IMPRINT",EDGE,{"derivedFrom":sQuery(id+"F0.wireOp",EDGE,"E8.0.3.0")}),-1.0]])]});
            var Q69;
            Q69=makeQuery(id+"F0.imprint","IMPRINT",FACE,{"disambiguationData":[TD([[makeQuery(id+"F0.imprint","IMPRINT",EDGE,{"derivedFrom":sQuery(id+"F0.wireOp",EDGE,"E8.0.2.0")}),-1.0]])]});
            var Q70;
            Q70=makeQuery(id+"F0.imprint","IMPRINT",FACE,{"disambiguationData":[TD([[makeQuery(id+"F0.imprint","IMPRINT",EDGE,{"derivedFrom":sQuery(id+"F0.wireOp",EDGE,"E8.0.1.0")}),-1.0]])]});
            extrude(context, id + "F1", {"entities" : qUnion([Q0, Q1, Q2, Q3, Q4, Q5, Q6, Q7, Q8, Q9, Q10, Q11, Q12, Q13, Q14, Q15, Q16, Q17, Q18, Q19, Q20, Q21, Q22, Q23, Q24, Q25, Q26, Q27, Q28, Q29, Q30, Q31, Q32, Q33, Q34, Q35, Q36, Q37, Q38, Q39, Q40, Q41, Q42, Q43, Q44, Q45, Q46, Q47, Q48, Q49, Q50, Q51, Q52, Q53, Q54, Q55, Q56, Q57, Q58, Q59, Q60, Q61, Q62, Q63, Q64, Q65, Q66, Q67, Q68, Q69, Q70]), "oppositeDirection" : true, "depth" : 1 * mm, "offsetDistance" : 25 * mm});
        }
    });
